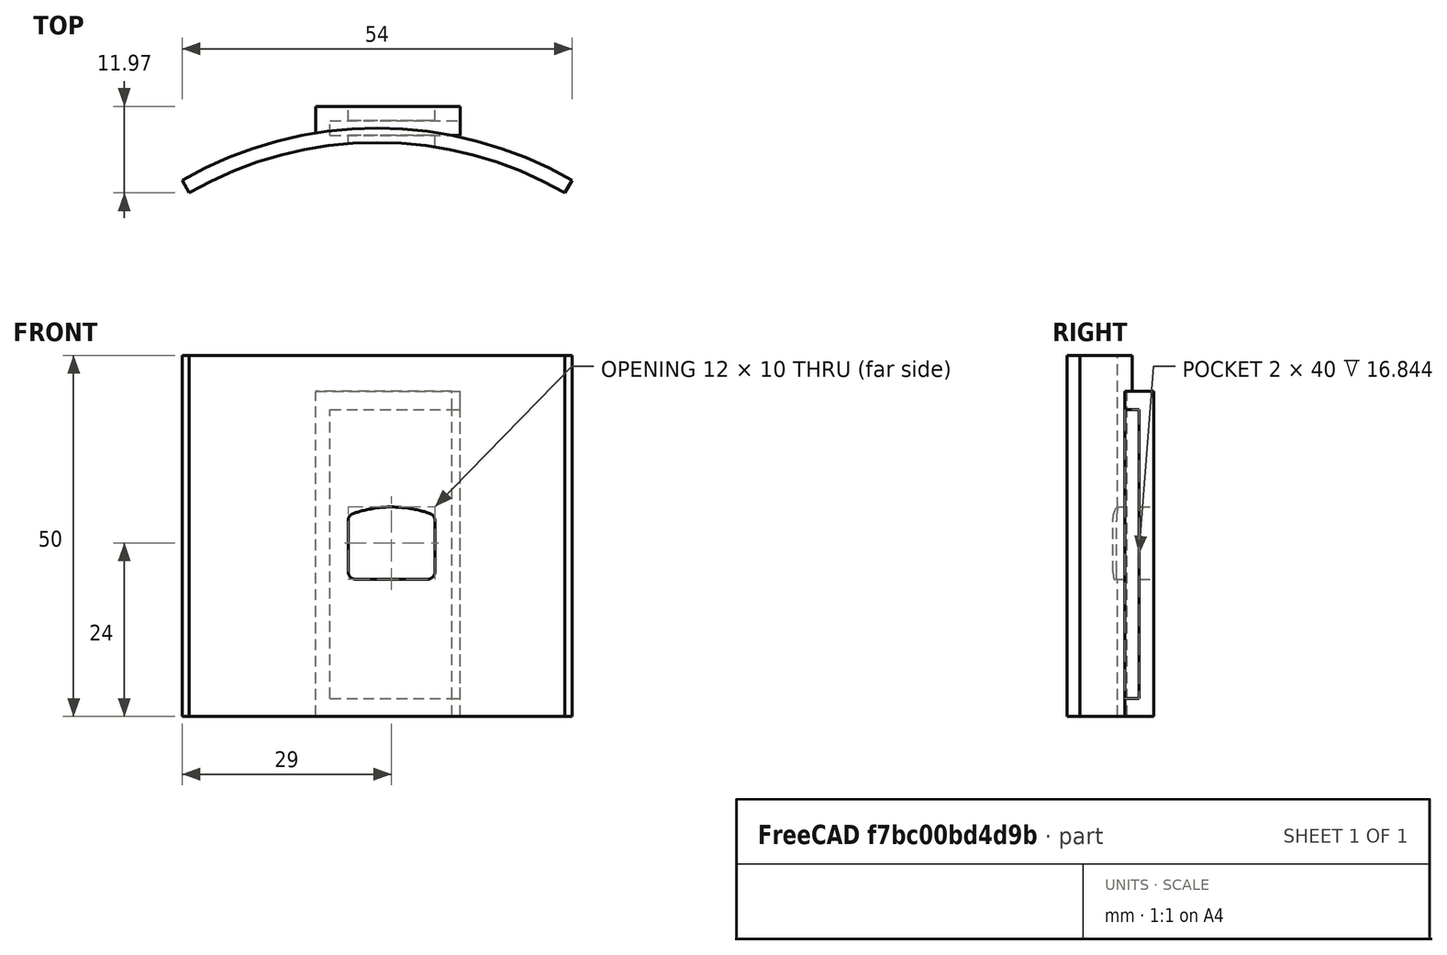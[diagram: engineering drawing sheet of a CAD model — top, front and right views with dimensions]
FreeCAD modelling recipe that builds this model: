
FCSTD DOCUMENT  (FreeCAD 0.16R4924 (Git))
Label: outer_latch_v2.1
License: All rights reserved
LicenseURL: http://en.wikipedia.org/wiki/All_rights_reserved
objects: Part::Cut×3, Part::MultiFuse×3, Part::Cylinder×2, Part::Box×2, Part::Feature×2, Part::Extrusion×2, Part::Thickness×1
note: 15 computed .brp shape members not serialized (recipe doc carries the construction recipe); baked Part::Feature solids carry a one-line shape summary decoded from their .brp

FEATURE [Part::Cylinder] Cylinder  label="bottle_wall"
  Angle = 60
  Height = 50
  Placement = pos=(8.5,-7,0) rot=(0,0,1;1.0472rad)
  Radius = 54
FEATURE [Part::Cylinder] Cylinder001  label="bottle_wall001"
  Angle = 60
  Height = 50
  Placement = pos=(8.5,-7,0) rot=(0,0,1;1.0472rad)
  Radius = 52
FEATURE [Part::Cut] Cut  label="final_bottle wall"
  Base = -> Cylinder
  Placement = pos=(0,-2,0) rot=(0,0,1;0rad)
  Tool = -> Cylinder001
FEATURE [Part::Box] Box001  label="latch"
  Height = 45
  Length = 20
  Placement = pos=(0,44,0) rot=(0,0,1;0rad)
  Width = 4
FEATURE [Part::MultiFuse] Fusion
  Shapes = -> [Cut,Box001]
FEATURE [Part::MultiFuse] Fusion001  label="wall_plus_latch"
  Shapes = -> [Fusion,Box001]
FEATURE [Part::Box] Box002  label="slot"
  Height = 40
  Length = 20
  Placement = pos=(2,44,2.5) rot=(0,0,1;0rad)
  Width = 2
FEATURE [Part::Feature] Common_cs001  label="pin_cs001"
  Placement = pos=(3.5,35,2) rot=(0,0,1;0rad)
  shape: bbox 10 x 2e-07 x 8 mm, 0 faces, 0 solids (baked)
FEATURE [Part::Extrusion] Extrude
  Base = -> Common_cs001
  Dir = (0,6,0)
  Solid = true
FEATURE [Part::Thickness] Thickness
  Faces = -> Extrude [Face7]
  Intersection = false
  Join = 0
  Mode = 0
  SelfIntersection = false
  Value = 1
FEATURE [Part::Feature] Common_cs002  label="pin_cs002"
  Placement = pos=(3.5,35,2) rot=(0,0,1;0rad)
  shape: bbox 10 x 2e-07 x 8 mm, 0 faces, 0 solids (baked)
FEATURE [Part::Extrusion] Extrude001
  Base = -> Common_cs002
  Dir = (0,6,0)
  Solid = true
FEATURE [Part::MultiFuse] Fusion002  label="pin opening"
  Placement = pos=(2,-3,18) rot=(0,0,1;0rad)
  Shapes = -> [Thickness,Extrude,Extrude001]
FEATURE [Part::Cut] Cut003
  Base = -> Fusion001
  Tool = -> Fusion002
FEATURE [Part::Cut] Cut004
  Base = -> Cut003
  Tool = -> Box002
